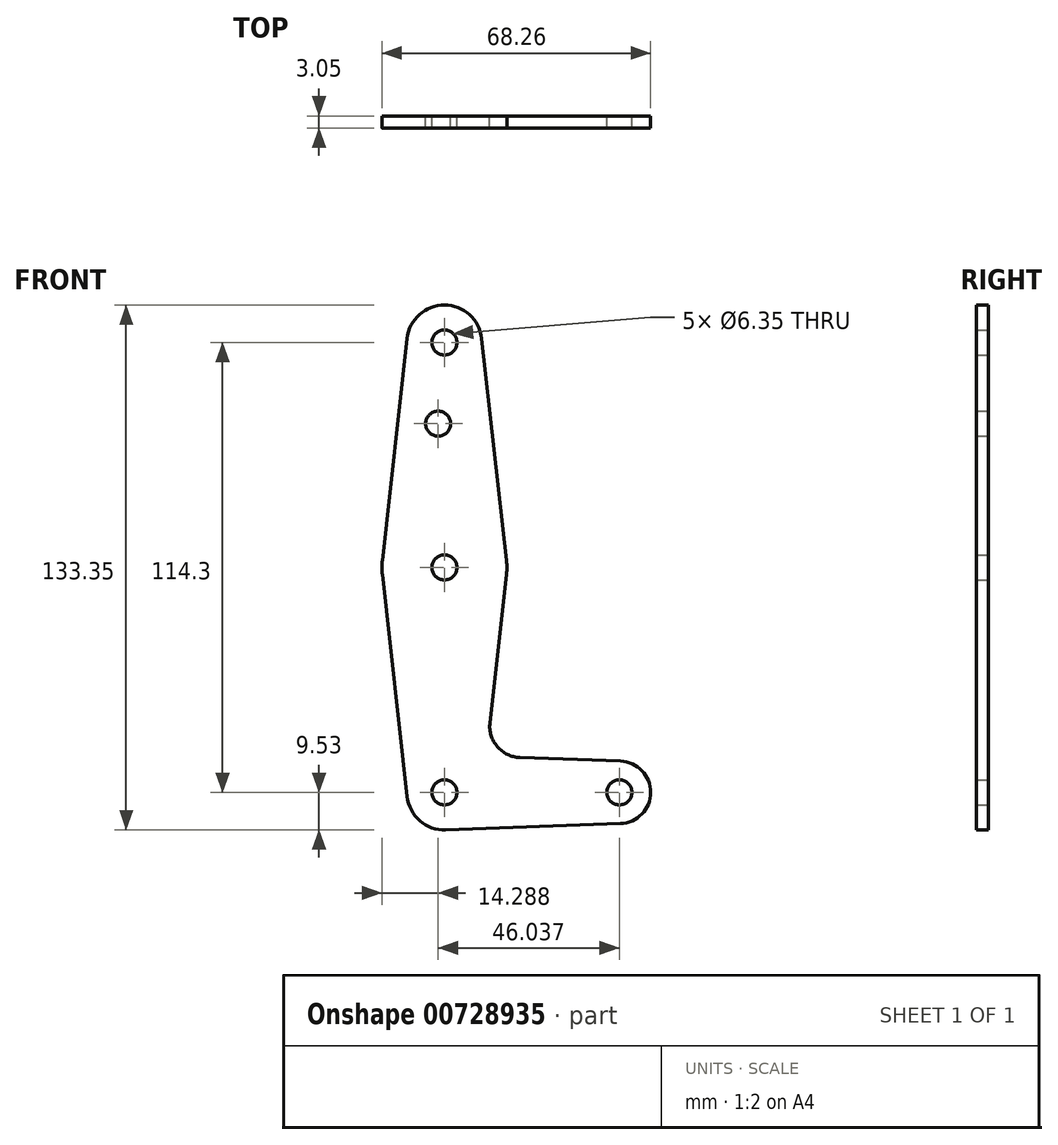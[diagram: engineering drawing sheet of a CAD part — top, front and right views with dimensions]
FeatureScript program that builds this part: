
annotation { "Feature Type Name" : "Feature", "Feature Type Description" : "" }
export const myFeature = defineFeature(function(context is Context, id is Id, definition is map)
    precondition{}
    {
        {
            var Q0;
            Q0=qCreatedBy(makeId("Front.planeOp"),FACE);
            var sketch = newSketch(context, id + "F0", { "sketchPlane" : qUnion([Q0])});
            skLineSegment(sketch, "E0", {"start": v(-59.45, 0) * mm, "end": v(-59.45, -63.5) * mm, "construction": true});
            skLineSegment(sketch, "E1", {"start": v(-59.45, -63.5) * mm, "end": v(-15, -63.5) * mm, "construction": true});
            skCircle(sketch, "E2", {"center": v(-59.45, -63.5) * mm, "radius": 9.53 * mm});
            skCircle(sketch, "E3", {"center": v(-15, -63.5) * mm, "radius": 7.94 * mm});
            skCircle(sketch, "E4", {"center": v(-59.45, -6.35) * mm, "radius": 15.88 * mm});
            skLineSegment(sketch, "E5", {"start": v(-59.45, 0) * mm, "end": v(-59.45, 50.8) * mm, "construction": true});
            skCircle(sketch, "E6", {"center": v(-59.45, 50.8) * mm, "radius": 9.53 * mm});
            skLineSegment(sketch, "E7", {"start": v(-49.99, 51.86) * mm, "end": v(-43.68, -4.59) * mm});
            skLineSegment(sketch, "E8", {"start": v(-43.68, -8.11) * mm, "end": v(-47.9, -45.83) * mm});
            skLineSegment(sketch, "E9", {"start": v(-59.11, -73.02) * mm, "end": v(-14.72, -71.43) * mm});
            skLineSegment(sketch, "E10", {"start": v(-40.28, -54.65) * mm, "end": v(-14.72, -55.57) * mm});
            skLineSegment(sketch, "E11", {"start": v(-68.92, -64.56) * mm, "end": v(-75.23, -8.11) * mm});
            skLineSegment(sketch, "E12", {"start": v(-68.92, 51.86) * mm, "end": v(-75.23, -4.59) * mm});
            skCircle(sketch, "E13", {"center": v(-59.45, 50.8) * mm, "radius": 3.18 * mm});
            skCircle(sketch, "E14", {"center": v(-59.45, -6.35) * mm, "radius": 3.18 * mm});
            skCircle(sketch, "E15", {"center": v(-59.45, -63.5) * mm, "radius": 3.18 * mm});
            skCircle(sketch, "E16", {"center": v(-15, -63.5) * mm, "radius": 3.18 * mm});
            skCircle(sketch, "E17", {"center": v(-61.04, 30.18) * mm, "radius": 3.18 * mm});
            skArc(sketch, "E18.filletArc", {"start": v(-47.9, -45.83) * mm, "mid": v(-46.01, -51.9) * mm, "end": v(-40.28, -54.65) * mm});
            skSolve(sketch);
        }
        {
            var Q0;
            Q0 = qSketchRegion(id + "F0", true);
            extrude(context, id + "F1", {"entities" : qUnion([Q0]), "depth" : 3.05 * mm, "offsetDistance" : 25.4 * mm});
        }
    });
